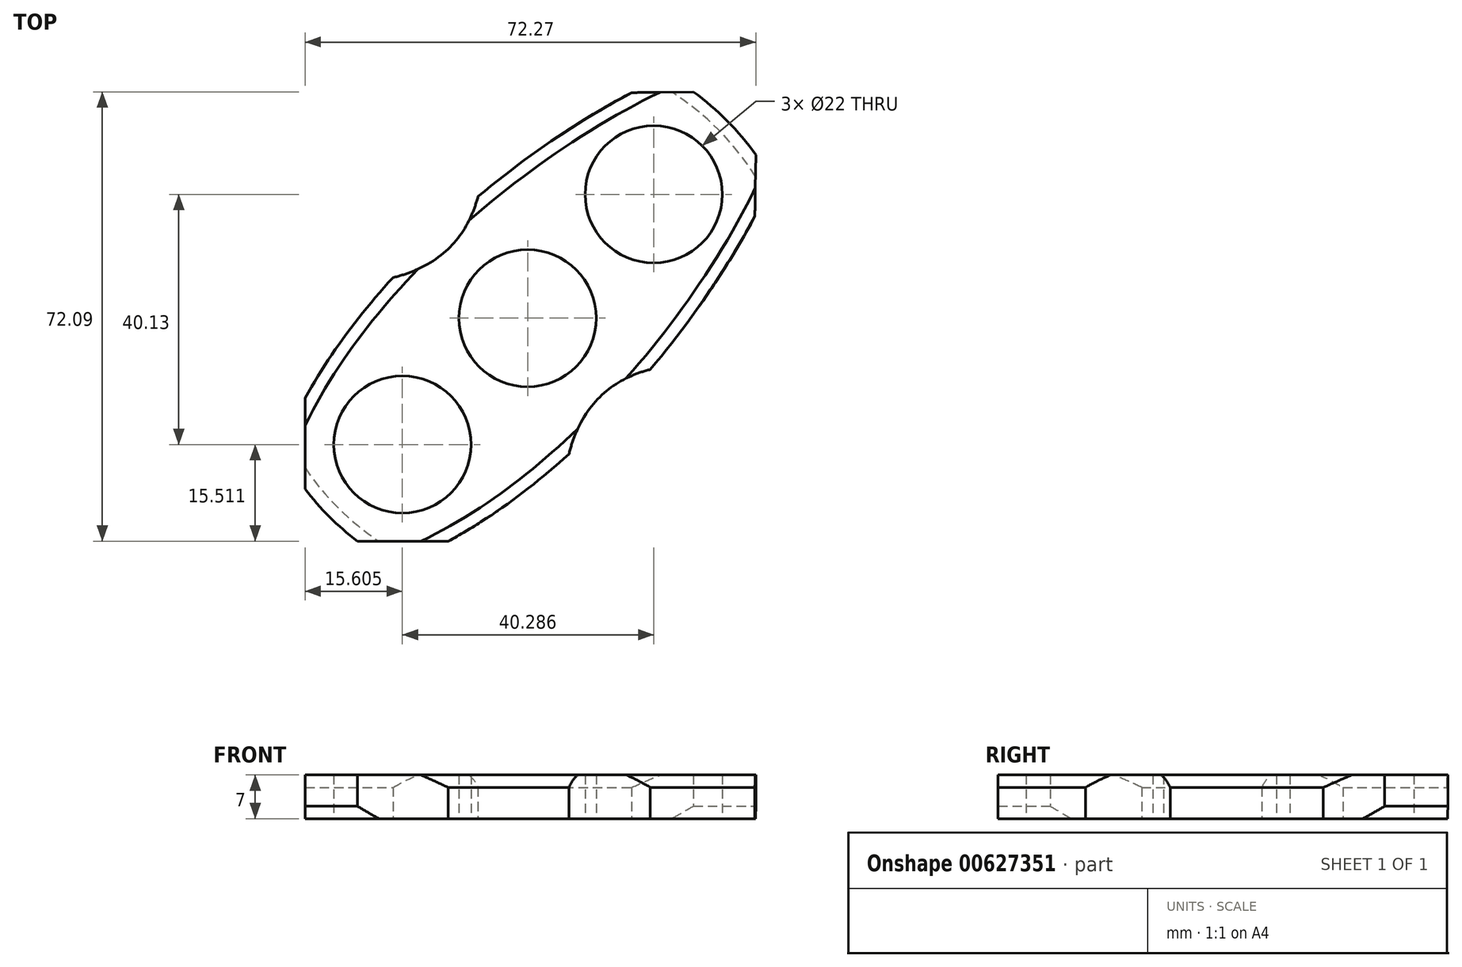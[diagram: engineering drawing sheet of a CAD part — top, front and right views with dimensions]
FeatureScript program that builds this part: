
annotation { "Feature Type Name" : "Feature", "Feature Type Description" : "" }
export const myFeature = defineFeature(function(context is Context, id is Id, definition is map)
    precondition{}
    {
        {
            var Q0;
            Q0=qCreatedBy(makeId("Front.planeOp"),FACE);
            var sketch = newSketch(context, id + "F0", { "sketchPlane" : qUnion([Q0])});
            skLineSegment(sketch, "E0", {"start": v(0, 0) * mm, "end": v(0, 50) * mm, "construction": true});
            skLineSegment(sketch, "E1", {"start": v(0, 0) * mm, "end": v(22, 0) * mm, "construction": true});
            skPoint(sketch, "E2.endSnap0", {"position": v(11, 0) * mm});
            skLineSegment(sketch, "E3", {"start": v(0, 7) * mm, "end": v(0, 0) * mm});
            skLineSegment(sketch, "E4", {"start": v(22, 0) * mm, "end": v(22, 7) * mm});
            skLineSegment(sketch, "E5", {"start": v(22, 7) * mm, "end": v(11, 7) * mm});
            skLineSegment(sketch, "E6", {"start": v(11, 7) * mm, "end": v(11, 0) * mm});
            skLineSegment(sketch, "E7", {"start": v(0, 0) * mm, "end": v(45, 0) * mm});
            skLineSegment(sketch, "E8", {"start": v(22, 7) * mm, "end": v(45, 7) * mm});
            skLineSegment(sketch, "E9", {"start": v(45, 7) * mm, "end": v(45, 0) * mm});
            skSolve(sketch);
        }
        {
            var Q0;
            Q0 = qSketchRegion(id + "F0", true);
            var Q1;
            Q1=sQuery(id+"F0.wireOp",EDGE,"E0");
            revolve(context, id + "F1", {"entities" : qUnion([Q0]), "axis" : qUnion([Q1]), "revolveType" : RevolveType.FULL});
        }
        {
            var Q0;
            Q0=qCreatedBy(makeId("Top.planeOp"),FACE);
            var sketch = newSketch(context, id + "F2", { "sketchPlane" : qUnion([Q0])});
            skLineSegment(sketch, "E10", {"start": v(0, 0) * mm, "end": v(54.99, 0) * mm, "construction": true});
            skLineSegment(sketch, "E11", {"start": v(54.99, 0) * mm, "end": v(0, 54.4) * mm, "construction": true});
            skLineSegment(sketch, "E12", {"start": v(0, 54.4) * mm, "end": v(0, 0) * mm, "construction": true});
            skLineSegment(sketch, "E13", {"start": v(0, 0) * mm, "end": v(0, -54.99) * mm, "construction": true});
            skLineSegment(sketch, "E14", {"start": v(0, -54.99) * mm, "end": v(-54.8, 0) * mm, "construction": true});
            skLineSegment(sketch, "E15", {"start": v(-54.8, 0) * mm, "end": v(0, 0) * mm, "construction": true});
            skLineSegment(sketch, "E16", {"start": v(0, 54.4) * mm, "end": v(-54.8, 0) * mm, "construction": true});
            skLineSegment(sketch, "E17", {"start": v(0, -54.99) * mm, "end": v(54.99, 0) * mm, "construction": true});
            skLineSegment(sketch, "E18", {"start": v(27.5, 27.2) * mm, "end": v(-27.4, -27.5) * mm, "construction": true});
            skPoint(sketch, "E18.endSnap0", {"position": v(-27.4, -27.5) * mm});
            skSolve(sketch);
        }
        {
            var Q0;
            Q0=qCreatedBy(makeId("Top.planeOp"),FACE);
            var sketch = newSketch(context, id + "F3", { "sketchPlane" : qUnion([Q0])});
            skCircle(sketch, "E19", {"center": v(-20.08, -20.27) * mm, "radius": 11 * mm});
            skCircle(sketch, "E20", {"center": v(20.21, 19.86) * mm, "radius": 11 * mm});
            skSolve(sketch);
        }
        {
            var Q0;
            Q0=qCreatedBy(makeId("Top.planeOp"),FACE);
            var sketch = newSketch(context, id + "F4", { "sketchPlane" : qUnion([Q0])});
            skFitSpline(sketch, "E21", {"points": [v(-24.11, -40.7) * mm, v(40.3, 24.4) * mm], "startDerivative": vector(82.68, 26.3) * mm, "endDerivative": vector(31.01, 73.05) * mm});
            skLineSegment(sketch, "E22", {"start": v(-27.41, -27.29) * mm, "end": v(-52.34, -51.95) * mm, "construction": true});
            skFitSpline(sketch, "E23", {"points": [v(40.3, 24.4) * mm, v(39.47, 36.95) * mm], "startDerivative": vector(26.26, 16.58) * mm, "endDerivative": vector(-2.3, 28.1) * mm});
            skFitSpline(sketch, "E24", {"points": [v(-24.11, -40.7) * mm, v(-36.76, -39.08) * mm], "startDerivative": vector(-20.32, -27.96) * mm, "endDerivative": vector(-29.31, 5.86) * mm});
            skLineSegment(sketch, "E25", {"start": v(-36.76, -39.08) * mm, "end": v(31.6, -85.9) * mm});
            skLineSegment(sketch, "E26", {"start": v(31.6, -85.9) * mm, "end": v(91.97, 5.08) * mm});
            skLineSegment(sketch, "E27", {"start": v(91.97, 5.08) * mm, "end": v(39.47, 36.95) * mm});
            skFitSpline(sketch, "E28.MirrorCS", {"points": [v(-40.6, -24.16) * mm, v(24.75, 40.01) * mm], "startDerivative": vector(26.58, 82.59) * mm, "endDerivative": vector(73.15, 30.75) * mm});
            skFitSpline(sketch, "E29.MirrorCS", {"points": [v(24.75, 40.01) * mm, v(37.28, 39.15) * mm], "startDerivative": vector(16.68, 26.2) * mm, "endDerivative": vector(28.1, -2.4) * mm});
            skLineSegment(sketch, "E30.MirrorCS", {"start": v(5.6, 91.76) * mm, "end": v(37.28, 39.15) * mm});
            skLineSegment(sketch, "E31.MirrorCS", {"start": v(-85.6, 31.72) * mm, "end": v(5.6, 91.76) * mm});
            skLineSegment(sketch, "E32.MirrorCS", {"start": v(-39.02, -36.81) * mm, "end": v(-85.6, 31.72) * mm});
            skFitSpline(sketch, "E33.MirrorCS", {"points": [v(-40.6, -24.16) * mm, v(-39.02, -36.81) * mm], "startDerivative": vector(-28.03, -20.23) * mm, "endDerivative": vector(5.76, -29.33) * mm});
            skSolve(sketch);
        }
        {
            var Q0;
            Q0=qCreatedBy(makeId("Top.planeOp"),FACE);
            var sketch = newSketch(context, id + "F5", { "sketchPlane" : qUnion([Q0])});
            skFitSpline(sketch, "E34", {"points": [v(45.12, -10.28) * mm, v(7.9, -47.04) * mm], "startDerivative": vector(-8.27, 0) * mm, "endDerivative": vector(38.6, -165.4) * mm});
            skLineSegment(sketch, "E35", {"start": v(7.9, -47.04) * mm, "end": v(56.37, -47.04) * mm});
            skLineSegment(sketch, "E36", {"start": v(56.37, -47.04) * mm, "end": v(45.12, -10.28) * mm});
            skFitSpline(sketch, "E37.MirrorCS", {"points": [v(-9.93, 44.96) * mm, v(-46.82, 7.87) * mm], "startDerivative": vector(-0.03, -8.27) * mm, "endDerivative": vector(-165.27, 39.18) * mm});
            skLineSegment(sketch, "E38.MirrorCS", {"start": v(-46.64, 56.34) * mm, "end": v(-9.93, 44.96) * mm});
            skLineSegment(sketch, "E39.MirrorCS", {"start": v(-46.82, 7.87) * mm, "end": v(-46.64, 56.34) * mm});
            skSolve(sketch);
        }
        {
            var Q0;
            Q0 = qSketchRegion(id + "F3", true);
            extrude(context, id + "F6", {"entities" : qUnion([Q0]), "operationType" : NewBodyOperationType.REMOVE, "depth" : 25 * mm, "offsetDistance" : 25 * mm});
        }
        {
            var Q0;
            Q0 = qSketchRegion(id + "F4", true);
            extrude(context, id + "F7", {"entities" : qUnion([Q0]), "operationType" : NewBodyOperationType.REMOVE, "depth" : 25 * mm, "offsetDistance" : 25 * mm});
        }
        {
            var Q0;
            Q0 = qSketchRegion(id + "F5", true);
            extrude(context, id + "F8", {"entities" : qUnion([Q0]), "operationType" : NewBodyOperationType.REMOVE, "depth" : 25 * mm, "offsetDistance" : 25 * mm});
        }
        {
            var Q0;
            Q0=makeQuery(id+"F8.boolean.opBoolean","INTERSECT",EDGE,{"derivedFrom":[makeQuery(id+"F1.opRevolve","SWEPT_FACE",FACE,{"disambiguationData":[OSD([sQuery(id+"F0.wireOp",EDGE,"E5"),sQuery(id+"F0.wireOp",EDGE,"gYPfrRNB-XZMY-J8aB-PTPO-REFipaiEdQMu")])]}),makeQuery(id+"F8.opExtrude","SWEPT_FACE",FACE,{"disambiguationData":[OSD([sQuery(id+"F5.wireOp",EDGE,"6a314824-d33c-41ba-95fc-e3e31f57a93c0.MirrorCS")])]})]});
            var Q1;
            {var subQ0=makeQuery(id+"F1.opRevolve","SWEPT_FACE",FACE,{"disambiguationData":[OSD([sQuery(id+"F0.wireOp",EDGE,"E5"),sQuery(id+"F0.wireOp",EDGE,"gYPfrRNB-XZMY-J8aB-PTPO-REFipaiEdQMu")])]});var subQ1=makeQuery(id+"F7.opExtrude","SWEPT_FACE",FACE,{"disambiguationData":[OSD([sQuery(id+"F4.wireOp",EDGE,"E28.MirrorCS")])]});Q1=makeQuery(id+"F8.boolean.opBoolean","SPLIT",EDGE,{"disambiguationData":[TD([makeQuery(id+"F7.boolean.opBoolean","COPY",FACE,{"derivedFrom":makeQuery(id+"F7.opExtrude","SWEPT_FACE",FACE,{"disambiguationData":[OSD([sQuery(id+"F4.wireOp",EDGE,"E29.MirrorCS")])]})})])],"derivedFrom":makeQuery(id+"F7.boolean.opBoolean","INTERSECT",EDGE,{"derivedFrom":[subQ0,subQ1]})});}
            var Q2;
            Q2=makeQuery(id+"F7.boolean.opBoolean","INTERSECT",EDGE,{"derivedFrom":[makeQuery(id+"F1.opRevolve","SWEPT_FACE",FACE,{"disambiguationData":[OSD([sQuery(id+"F0.wireOp",EDGE,"E5"),sQuery(id+"F0.wireOp",EDGE,"gYPfrRNB-XZMY-J8aB-PTPO-REFipaiEdQMu")])]}),makeQuery(id+"F7.opExtrude","SWEPT_FACE",FACE,{"disambiguationData":[OSD([sQuery(id+"F4.wireOp",EDGE,"E29.MirrorCS")])]})]});
            var Q3;
            Q3=makeQuery(id+"F7.boolean.opBoolean","INTERSECT",EDGE,{"derivedFrom":[makeQuery(id+"F1.opRevolve","SWEPT_FACE",FACE,{"disambiguationData":[OSD([sQuery(id+"F0.wireOp",EDGE,"E5"),sQuery(id+"F0.wireOp",EDGE,"gYPfrRNB-XZMY-J8aB-PTPO-REFipaiEdQMu")])]}),makeQuery(id+"F7.opExtrude","SWEPT_FACE",FACE,{"disambiguationData":[OSD([sQuery(id+"F4.wireOp",EDGE,"E23")])]})]});
            var Q4;
            {var subQ0=makeQuery(id+"F1.opRevolve","SWEPT_FACE",FACE,{"disambiguationData":[OSD([sQuery(id+"F0.wireOp",EDGE,"E5"),sQuery(id+"F0.wireOp",EDGE,"gYPfrRNB-XZMY-J8aB-PTPO-REFipaiEdQMu")])]});var subQ1=makeQuery(id+"F7.opExtrude","SWEPT_FACE",FACE,{"disambiguationData":[OSD([sQuery(id+"F4.wireOp",EDGE,"E21")])]});Q4=makeQuery(id+"F8.boolean.opBoolean","SPLIT",EDGE,{"disambiguationData":[TD([makeQuery(id+"F7.boolean.opBoolean","COPY",FACE,{"derivedFrom":makeQuery(id+"F7.opExtrude","SWEPT_FACE",FACE,{"disambiguationData":[OSD([sQuery(id+"F4.wireOp",EDGE,"E23")])]})})])],"derivedFrom":makeQuery(id+"F7.boolean.opBoolean","INTERSECT",EDGE,{"derivedFrom":[subQ0,subQ1]})});}
            var Q5;
            Q5=makeQuery(id+"F8.boolean.opBoolean","INTERSECT",EDGE,{"derivedFrom":[makeQuery(id+"F1.opRevolve","SWEPT_FACE",FACE,{"disambiguationData":[OSD([sQuery(id+"F0.wireOp",EDGE,"E5"),sQuery(id+"F0.wireOp",EDGE,"gYPfrRNB-XZMY-J8aB-PTPO-REFipaiEdQMu")])]}),makeQuery(id+"F8.opExtrude","SWEPT_FACE",FACE,{"disambiguationData":[OSD([sQuery(id+"F5.wireOp",EDGE,"df86577d-89be-4ed1-9085-acb398cfc0aa")])]})]});
            var Q6;
            {var subQ0=makeQuery(id+"F1.opRevolve","SWEPT_FACE",FACE,{"disambiguationData":[OSD([sQuery(id+"F0.wireOp",EDGE,"E5"),sQuery(id+"F0.wireOp",EDGE,"gYPfrRNB-XZMY-J8aB-PTPO-REFipaiEdQMu")])]});var subQ1=makeQuery(id+"F7.opExtrude","SWEPT_FACE",FACE,{"disambiguationData":[OSD([sQuery(id+"F4.wireOp",EDGE,"E21")])]});Q6=makeQuery(id+"F8.boolean.opBoolean","SPLIT",EDGE,{"disambiguationData":[TD([makeQuery(id+"F7.boolean.opBoolean","COPY",FACE,{"derivedFrom":makeQuery(id+"F7.opExtrude","SWEPT_FACE",FACE,{"disambiguationData":[OSD([sQuery(id+"F4.wireOp",EDGE,"E24")])]})})])],"derivedFrom":makeQuery(id+"F7.boolean.opBoolean","INTERSECT",EDGE,{"derivedFrom":[subQ0,subQ1]})});}
            var Q7;
            Q7=makeQuery(id+"F7.boolean.opBoolean","INTERSECT",EDGE,{"derivedFrom":[makeQuery(id+"F1.opRevolve","SWEPT_FACE",FACE,{"disambiguationData":[OSD([sQuery(id+"F0.wireOp",EDGE,"E5"),sQuery(id+"F0.wireOp",EDGE,"gYPfrRNB-XZMY-J8aB-PTPO-REFipaiEdQMu")])]}),makeQuery(id+"F7.opExtrude","SWEPT_FACE",FACE,{"disambiguationData":[OSD([sQuery(id+"F4.wireOp",EDGE,"E24")])]})]});
            var Q8;
            Q8=makeQuery(id+"F7.boolean.opBoolean","INTERSECT",EDGE,{"derivedFrom":[makeQuery(id+"F1.opRevolve","SWEPT_FACE",FACE,{"disambiguationData":[OSD([sQuery(id+"F0.wireOp",EDGE,"E5"),sQuery(id+"F0.wireOp",EDGE,"gYPfrRNB-XZMY-J8aB-PTPO-REFipaiEdQMu")])]}),makeQuery(id+"F7.opExtrude","SWEPT_FACE",FACE,{"disambiguationData":[OSD([sQuery(id+"F4.wireOp",EDGE,"E33.MirrorCS")])]})]});
            var Q9;
            {var subQ0=makeQuery(id+"F1.opRevolve","SWEPT_FACE",FACE,{"disambiguationData":[OSD([sQuery(id+"F0.wireOp",EDGE,"E5"),sQuery(id+"F0.wireOp",EDGE,"gYPfrRNB-XZMY-J8aB-PTPO-REFipaiEdQMu")])]});var subQ1=makeQuery(id+"F7.opExtrude","SWEPT_FACE",FACE,{"disambiguationData":[OSD([sQuery(id+"F4.wireOp",EDGE,"E28.MirrorCS")])]});Q9=makeQuery(id+"F8.boolean.opBoolean","SPLIT",EDGE,{"disambiguationData":[TD([makeQuery(id+"F7.boolean.opBoolean","COPY",FACE,{"derivedFrom":makeQuery(id+"F7.opExtrude","SWEPT_FACE",FACE,{"disambiguationData":[OSD([sQuery(id+"F4.wireOp",EDGE,"E33.MirrorCS")])]})})])],"derivedFrom":makeQuery(id+"F7.boolean.opBoolean","INTERSECT",EDGE,{"derivedFrom":[subQ0,subQ1]})});}
            var Q10;
            Q10=makeQuery(id+"F7.boolean.opBoolean","COPY",EDGE,{"derivedFrom":makeQuery(id+"F7.opExtrude","CAP_EDGE",EDGE,{"disambiguationData":[OSD([sQuery(id+"F4.wireOp",EDGE,"E24")])],"isStart":true})});
            var Q11;
            {var subQ0=sQuery(id+"F4.wireOp",EDGE,"E21");Q11=makeQuery(id+"F8.boolean.opBoolean","SPLIT",EDGE,{"disambiguationData":[TD([makeQuery(id+"F7.boolean.opBoolean","COPY",FACE,{"derivedFrom":makeQuery(id+"F7.opExtrude","SWEPT_FACE",FACE,{"disambiguationData":[OSD([sQuery(id+"F4.wireOp",EDGE,"E24")])]})})])],"derivedFrom":makeQuery(id+"F7.boolean.opBoolean","COPY",EDGE,{"derivedFrom":makeQuery(id+"F7.opExtrude","CAP_EDGE",EDGE,{"disambiguationData":[OSD([subQ0])],"isStart":true})})});}
            var Q12;
            Q12=makeQuery(id+"F8.boolean.opBoolean","COPY",EDGE,{"derivedFrom":makeQuery(id+"F8.opExtrude","CAP_EDGE",EDGE,{"disambiguationData":[OSD([sQuery(id+"F5.wireOp",EDGE,"df86577d-89be-4ed1-9085-acb398cfc0aa")])],"isStart":true})});
            var Q13;
            {var subQ0=sQuery(id+"F4.wireOp",EDGE,"E21");Q13=makeQuery(id+"F8.boolean.opBoolean","SPLIT",EDGE,{"disambiguationData":[TD([makeQuery(id+"F7.boolean.opBoolean","COPY",FACE,{"derivedFrom":makeQuery(id+"F7.opExtrude","SWEPT_FACE",FACE,{"disambiguationData":[OSD([sQuery(id+"F4.wireOp",EDGE,"E23")])]})})])],"derivedFrom":makeQuery(id+"F7.boolean.opBoolean","COPY",EDGE,{"derivedFrom":makeQuery(id+"F7.opExtrude","CAP_EDGE",EDGE,{"disambiguationData":[OSD([subQ0])],"isStart":true})})});}
            var Q14;
            Q14=makeQuery(id+"F7.boolean.opBoolean","COPY",EDGE,{"derivedFrom":makeQuery(id+"F7.opExtrude","CAP_EDGE",EDGE,{"disambiguationData":[OSD([sQuery(id+"F4.wireOp",EDGE,"E23")])],"isStart":true})});
            var Q15;
            Q15=makeQuery(id+"F7.boolean.opBoolean","COPY",EDGE,{"derivedFrom":makeQuery(id+"F7.opExtrude","CAP_EDGE",EDGE,{"disambiguationData":[OSD([sQuery(id+"F4.wireOp",EDGE,"E29.MirrorCS")])],"isStart":true})});
            var Q16;
            {var subQ0=sQuery(id+"F4.wireOp",EDGE,"E28.MirrorCS");Q16=makeQuery(id+"F8.boolean.opBoolean","SPLIT",EDGE,{"disambiguationData":[TD([makeQuery(id+"F7.boolean.opBoolean","COPY",FACE,{"derivedFrom":makeQuery(id+"F7.opExtrude","SWEPT_FACE",FACE,{"disambiguationData":[OSD([sQuery(id+"F4.wireOp",EDGE,"E29.MirrorCS")])]})})])],"derivedFrom":makeQuery(id+"F7.boolean.opBoolean","COPY",EDGE,{"derivedFrom":makeQuery(id+"F7.opExtrude","CAP_EDGE",EDGE,{"disambiguationData":[OSD([subQ0])],"isStart":true})})});}
            var Q17;
            Q17=makeQuery(id+"F8.boolean.opBoolean","COPY",EDGE,{"derivedFrom":makeQuery(id+"F8.opExtrude","CAP_EDGE",EDGE,{"disambiguationData":[OSD([sQuery(id+"F5.wireOp",EDGE,"6a314824-d33c-41ba-95fc-e3e31f57a93c0.MirrorCS")])],"isStart":true})});
            var Q18;
            {var subQ0=sQuery(id+"F4.wireOp",EDGE,"E28.MirrorCS");Q18=makeQuery(id+"F8.boolean.opBoolean","SPLIT",EDGE,{"disambiguationData":[TD([makeQuery(id+"F7.boolean.opBoolean","COPY",FACE,{"derivedFrom":makeQuery(id+"F7.opExtrude","SWEPT_FACE",FACE,{"disambiguationData":[OSD([sQuery(id+"F4.wireOp",EDGE,"E33.MirrorCS")])]})})])],"derivedFrom":makeQuery(id+"F7.boolean.opBoolean","COPY",EDGE,{"derivedFrom":makeQuery(id+"F7.opExtrude","CAP_EDGE",EDGE,{"disambiguationData":[OSD([subQ0])],"isStart":true})})});}
            var Q19;
            Q19=makeQuery(id+"F7.boolean.opBoolean","COPY",EDGE,{"derivedFrom":makeQuery(id+"F7.opExtrude","CAP_EDGE",EDGE,{"disambiguationData":[OSD([sQuery(id+"F4.wireOp",EDGE,"E33.MirrorCS")])],"isStart":true})});
            var Q20;
            {var subQ0=sQuery(id+"F0.wireOp",EDGE,"E7");var subQ1=sQuery(id+"F0.wireOp",EDGE,"8882b417-c3fe-4d16-96ce-da570ab99f77");Q20=makeQuery(id+"F7.boolean.opBoolean","SPLIT",EDGE,{"disambiguationData":[TD([makeQuery(id+"F7.opExtrude","SWEPT_FACE",FACE,{"disambiguationData":[OSD([sQuery(id+"F4.wireOp",EDGE,"E24")])]})])],"derivedFrom":makeQuery(id+"F1.opRevolve","SWEPT_EDGE",EDGE,{"disambiguationData":[OSD([subQ0,subQ1])]})});}
            var Q21;
            {var subQ0=sQuery(id+"F0.wireOp",EDGE,"gYPfrRNB-XZMY-J8aB-PTPO-REFipaiEdQMu");var subQ1=sQuery(id+"F0.wireOp",EDGE,"8882b417-c3fe-4d16-96ce-da570ab99f77");Q21=makeQuery(id+"F7.boolean.opBoolean","SPLIT",EDGE,{"disambiguationData":[TD([makeQuery(id+"F7.opExtrude","SWEPT_FACE",FACE,{"disambiguationData":[OSD([sQuery(id+"F4.wireOp",EDGE,"E24")])]})])],"derivedFrom":makeQuery(id+"F1.opRevolve","SWEPT_EDGE",EDGE,{"disambiguationData":[OSD([subQ0,subQ1])]})});}
            var Q22;
            {var subQ0=sQuery(id+"F0.wireOp",EDGE,"gYPfrRNB-XZMY-J8aB-PTPO-REFipaiEdQMu");var subQ1=sQuery(id+"F0.wireOp",EDGE,"8882b417-c3fe-4d16-96ce-da570ab99f77");Q22=makeQuery(id+"F7.boolean.opBoolean","SPLIT",EDGE,{"disambiguationData":[TD([makeQuery(id+"F7.opExtrude","SWEPT_FACE",FACE,{"disambiguationData":[OSD([sQuery(id+"F4.wireOp",EDGE,"E23")])]})])],"derivedFrom":makeQuery(id+"F1.opRevolve","SWEPT_EDGE",EDGE,{"disambiguationData":[OSD([subQ0,subQ1])]})});}
            var Q23;
            {var subQ0=sQuery(id+"F0.wireOp",EDGE,"E7");var subQ1=sQuery(id+"F0.wireOp",EDGE,"8882b417-c3fe-4d16-96ce-da570ab99f77");Q23=makeQuery(id+"F7.boolean.opBoolean","SPLIT",EDGE,{"disambiguationData":[TD([makeQuery(id+"F7.opExtrude","SWEPT_FACE",FACE,{"disambiguationData":[OSD([sQuery(id+"F4.wireOp",EDGE,"E23")])]})])],"derivedFrom":makeQuery(id+"F1.opRevolve","SWEPT_EDGE",EDGE,{"disambiguationData":[OSD([subQ0,subQ1])]})});}
            var Q24;
            Q24=makeQuery(id+"F8.boolean.opBoolean","SPLIT",EDGE,{"disambiguationData":[OD(0.0)],"derivedFrom":makeQuery(id+"F7.boolean.opBoolean","COPY",EDGE,{"derivedFrom":makeQuery(id+"F7.opExtrude","CAP_EDGE",EDGE,{"disambiguationData":[OSD([sQuery(id+"F4.wireOp",EDGE,"E21")])],"isStart":true})})});
            var Q25;
            Q25=makeQuery(id+"F8.boolean.opBoolean","SPLIT",EDGE,{"disambiguationData":[OD(1.0)],"derivedFrom":makeQuery(id+"F7.boolean.opBoolean","COPY",EDGE,{"derivedFrom":makeQuery(id+"F7.opExtrude","CAP_EDGE",EDGE,{"disambiguationData":[OSD([sQuery(id+"F4.wireOp",EDGE,"E21")])],"isStart":true})})});
            var Q26;
            Q26=makeQuery(id+"F8.boolean.opBoolean","COPY",EDGE,{"derivedFrom":makeQuery(id+"F8.opExtrude","CAP_EDGE",EDGE,{"disambiguationData":[OSD([sQuery(id+"F5.wireOp",EDGE,"E34")])],"isStart":true})});
            var Q27;
            Q27=makeQuery(id+"F8.boolean.opBoolean","SPLIT",EDGE,{"disambiguationData":[OD(1.0)],"derivedFrom":makeQuery(id+"F7.boolean.opBoolean","COPY",EDGE,{"derivedFrom":makeQuery(id+"F7.opExtrude","CAP_EDGE",EDGE,{"disambiguationData":[OSD([sQuery(id+"F4.wireOp",EDGE,"E28.MirrorCS")])],"isStart":true})})});
            var Q28;
            Q28=makeQuery(id+"F8.boolean.opBoolean","SPLIT",EDGE,{"disambiguationData":[OD(0.0)],"derivedFrom":makeQuery(id+"F7.boolean.opBoolean","COPY",EDGE,{"derivedFrom":makeQuery(id+"F7.opExtrude","CAP_EDGE",EDGE,{"disambiguationData":[OSD([sQuery(id+"F4.wireOp",EDGE,"E28.MirrorCS")])],"isStart":true})})});
            var Q29;
            Q29=makeQuery(id+"F8.boolean.opBoolean","COPY",EDGE,{"derivedFrom":makeQuery(id+"F8.opExtrude","CAP_EDGE",EDGE,{"disambiguationData":[OSD([sQuery(id+"F5.wireOp",EDGE,"E37.MirrorCS")])],"isStart":true})});
            chamfer(context, id + "F9", {"entities" : qUnion([Q0, Q1, Q2, Q3, Q4, Q5, Q6, Q7, Q8, Q9, Q10, Q11, Q12, Q13, Q14, Q15, Q16, Q17, Q18, Q19, Q20, Q21, Q22, Q23, Q24, Q25, Q26, Q27, Q28, Q29]), "width" : 2 * mm, "tangentPropagation" : true});
        }
        {
            var Q0;
            Q0=qCreatedBy(makeId("Top.planeOp"),FACE);
            var sketch = newSketch(context, id + "F10", { "sketchPlane" : qUnion([Q0])});
            skLineSegment(sketch, "E40", {"start": v(-30, -35.78) * mm, "end": v(-7.95, -35.78) * mm});
            skLineSegment(sketch, "E41.MirrorCS", {"start": v(-35.7, -30.08) * mm, "end": v(-35.61, -8.02) * mm});
            skLineSegment(sketch, "E42", {"start": v(-27.25, 28.09) * mm, "end": v(27.2, -27.28) * mm, "construction": true});
            skLineSegment(sketch, "E43.MirrorCS", {"start": v(36.65, 29.77) * mm, "end": v(36.28, 7.72) * mm});
            skLineSegment(sketch, "E44", {"start": v(-7.95, -35.78) * mm, "end": v(-19.67, -54.39) * mm});
            skLineSegment(sketch, "E45", {"start": v(-19.67, -54.39) * mm, "end": v(-30.24, -44.74) * mm});
            skLineSegment(sketch, "E46", {"start": v(-30.24, -44.74) * mm, "end": v(-30, -35.78) * mm});
            skLineSegment(sketch, "E47.MirrorCS", {"start": v(36.28, 7.72) * mm, "end": v(55.09, 19.13) * mm});
            skLineSegment(sketch, "E48.MirrorCS", {"start": v(55.09, 19.13) * mm, "end": v(45.62, 29.85) * mm});
            skLineSegment(sketch, "E49.MirrorCS", {"start": v(45.62, 29.85) * mm, "end": v(36.65, 29.77) * mm});
            skLineSegment(sketch, "E50.MirrorCS", {"start": v(-35.61, -8.02) * mm, "end": v(-54.26, -19.67) * mm});
            skLineSegment(sketch, "E51.MirrorCS", {"start": v(-54.26, -19.67) * mm, "end": v(-44.65, -30.27) * mm});
            skLineSegment(sketch, "E52.MirrorCS", {"start": v(-44.65, -30.27) * mm, "end": v(-35.7, -30.08) * mm});
            skLineSegment(sketch, "E53.MirrorCS", {"start": v(30.1, 36.35) * mm, "end": v(8.04, 36.06) * mm});
            skLineSegment(sketch, "E54.MirrorCS", {"start": v(30.2, 45.31) * mm, "end": v(30.1, 36.35) * mm});
            skLineSegment(sketch, "E55.MirrorCS", {"start": v(19.51, 54.82) * mm, "end": v(30.2, 45.31) * mm});
            skLineSegment(sketch, "E56.MirrorCS", {"start": v(8.04, 36.06) * mm, "end": v(19.51, 54.82) * mm});
            skSolve(sketch);
        }
        {
            var Q0;
            Q0 = qSketchRegion(id + "F10", true);
            extrude(context, id + "F11", {"entities" : qUnion([Q0]), "operationType" : NewBodyOperationType.REMOVE, "depth" : 25 * mm, "offsetDistance" : 25 * mm});
        }
    });
